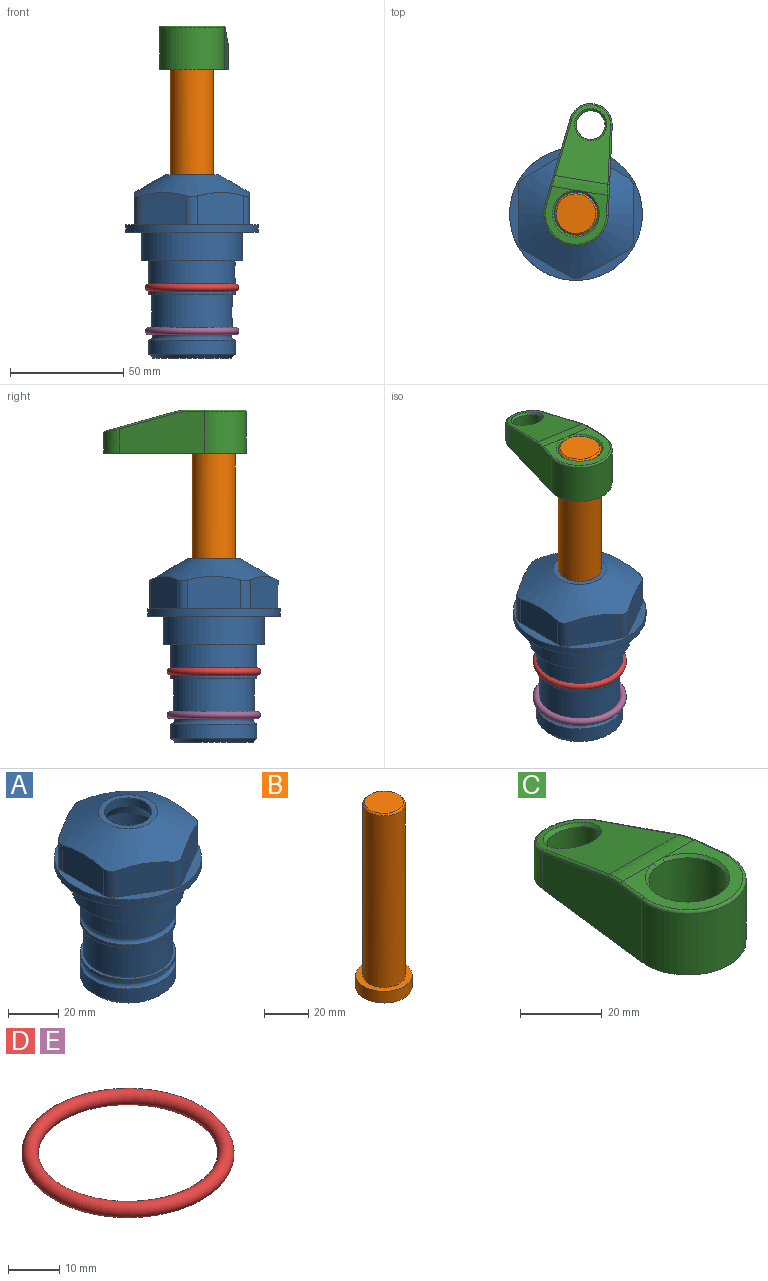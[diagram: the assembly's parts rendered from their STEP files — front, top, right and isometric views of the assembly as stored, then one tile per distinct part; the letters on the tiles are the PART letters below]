
ASSEMBLY  parts=5 mates=4
PART A: 36 faces, bbox 58.7x58.7x81 mm
  f0: cylinder r=17.78mm len=35.56mm, axis (0,0,1), area 1670.8mm2, adj f23,f24,f31
  f1: cylinder r=19.05mm len=38.1mm, axis (0,0,1), area 1191.9mm2, adj f26,f27,f30
  f2: plane 58.66x58.66mm, normal (0,0,-1), area 1150.6mm2, adj f3,f28
  f3: cylinder r=29.33mm len=58.66mm, axis (0,0,-1), area 585.1mm2, adj f2,f4
  f4: plane 58.66x58.66mm, normal (0,0,1), area 475.9mm2, adj f3,f5,f6,f7,f8,f9,f10,f11
  f5: plane 20.32x14.34mm, normal (-0.5,0.87,0), area 324.4mm2, adj f4,f15,f16,f17
  f6: plane 20.32x14.34mm, normal (0.5,0.87,0), area 324.4mm2, adj f4,f14,f15,f17
  f7: plane 23.48x14.34mm, normal (1,0,0), area 324.4mm2, adj f4,f13,f14,f17
  f8: plane 20.32x14.34mm, normal (0.5,-0.87,0), area 324.4mm2, adj f4,f12,f13,f17
  f9: plane 20.32x14.34mm, normal (-0.5,-0.87,0), area 324.4mm2, adj f4,f11,f12,f17
  f10: plane 23.48x14.34mm, normal (-1,0,0), area 324.4mm2, adj f4,f11,f16,f17
  f11: cylinder r=5.08mm len=12.85mm, axis (0,0,-1), area 67.2mm2, adj f4,f9,f10,f17
  f12: cylinder r=5.08mm len=12.85mm, axis (0,0,-1), area 67.2mm2, adj f4,f8,f9,f17
  f13: cylinder r=5.08mm len=12.85mm, axis (0,0,-1), area 67.2mm2, adj f4,f7,f8,f17
  f14: cylinder r=5.08mm len=12.85mm, axis (0,0,-1), area 67.2mm2, adj f4,f6,f7,f17
  f15: cylinder r=5.08mm len=12.85mm, axis (0,0,-1), area 67.2mm2, adj f4,f5,f6,f17
  f16: cylinder r=5.08mm len=12.85mm, axis (0,0,-1), area 67.2mm2, adj f4,f5,f10,f17
  f17: cone r=11.73mm half-angle=60deg, axis (0,0,-1), area 2071.8mm2, adj f5,f6,f7,f8,f9,f10,f11,f12
  f18: plane 23.46x23.46mm, normal (0,0,1), area 147.4mm2, adj f17,f35
  f19: plane 34.93x34.93mm, normal (0,0,-1), area 958mm2, adj f29
  f20: cylinder r=19.05mm len=38.1mm, axis (0,0,1), area 760.1mm2, adj f21,f29
  f21: torus R=19.05mm, axis (0,0,1), area 565.3mm2, adj f20,f22
  f22: cylinder r=19.05mm len=38.1mm, axis (0,0,1), area 190mm2, adj f21,f23
  f23: plane 38.1x38.1mm, normal (0,0,1), area 146.9mm2, adj f0,f22
  f24: plane 38.1x38.1mm, normal (0,0,-1), area 146.9mm2, adj f0,f25
  f25: cylinder r=19.05mm len=38.1mm, axis (0,0,1), area 190mm2, adj f24,f26
  f26: torus R=19.05mm, axis (0,0,1), area 565.3mm2, adj f1,f25
  f27: plane 44.45x44.45mm, normal (0,0,-1), area 411.7mm2, adj f1,f28
  f28: cylinder r=22.23mm len=44.45mm, axis (0,0,1), area 1773.5mm2, adj f2,f27
  f29: cone r=19.05mm half-angle=45deg, axis (0,0,1), area 257.5mm2, adj f19,f20
  f30: cylinder r=3.17mm len=6.75mm, axis (-1,0,0), area 128mm2, adj f1,f33
  f31: cylinder r=3.17mm len=6.35mm, axis (-1,0,0), area 102.5mm2, adj f0,f33
  f32: plane 25.4x25.4mm, normal (0,0,1), area 506.7mm2, adj f33
  f33: cylinder r=12.7mm len=66.42mm, axis (0,0,-1), area 5236.2mm2, adj f30,f31,f32,f34
  f34: cone r=9.53mm half-angle=30deg, axis (0,0,-1), area 443.4mm2, adj f33,f35
  f35: cylinder r=9.53mm len=19.05mm, axis (0,0,-1), area 240.9mm2, adj f18,f34
PART B: 6 faces, bbox 25.4x25.4x101.6 mm
  f0: plane 17.46x17.46mm, normal (0,0,1), area 239.5mm2, adj f5
  f1: plane 25.4x25.4mm, normal (0,0,-1), area 506.7mm2, adj f2
  f2: cylinder r=12.7mm len=25.4mm, axis (0,0,1), area 506.7mm2, adj f1,f3
  f3: plane 25.4x25.4mm, normal (0,0,1), area 221.7mm2, adj f2,f4
  f4: cylinder r=9.53mm len=94.46mm, axis (0,0,1), area 5653mm2, adj f3,f5
  f5: cone r=8.73mm half-angle=45deg, axis (0,0,-1), area 64.4mm2, adj f0,f4
PART C: 31 faces, bbox 31.7x65.5x19.8 mm
  f0: plane 39.12x18.26mm, normal (0.99,0.12,0), area 612.2mm2, adj f1,f4,f7,f11,f13,f15
  f1: cylinder r=9.53mm len=18.91mm, axis (0,0,-1), area 296.1mm2, adj f0,f2,f7,f17
  f2: plane 39.12x18.26mm, normal (-0.99,0.12,0), area 612.2mm2, adj f1,f4,f7,f12,f14,f16
  f3: cylinder r=6.35mm len=12.7mm, axis (0,0,-1), area 362.4mm2, adj f7,f18
  f4: cylinder r=14.29mm len=28.58mm, axis (0,0,-1), area 882.2mm2, adj f0,f2,f7,f10
  f5: cylinder r=9.53mm len=19.05mm, axis (0,0,-1), area 1092.6mm2, adj f7,f19,f20
  f6: plane 26.99x23.69mm, normal (0,0,1), area 216.2mm2, adj f9,f10,f11,f12,f19
  f7: plane 63.5x28.58mm, normal (0,0,-1), area 661.8mm2, adj f0,f1,f2,f3,f4,f5,f22,f23
  f8: plane 33.52x23.6mm, normal (0,0.26,0.97), area 486mm2, adj f9,f15,f16,f17,f18
  f9: cylinder r=19.05mm len=24.72mm, axis (1,0,0), area 120.4mm2, adj f6,f8,f13,f14,f20
  f10: torus R=13.49mm, axis (0,0,1), area 59mm2, adj f4,f6,f11,f12
  f11: cylinder r=0.79mm len=8.67mm, axis (0.12,-0.99,0), area 10.8mm2, adj f0,f6,f10,f13
  f12: cylinder r=0.79mm len=8.67mm, axis (0.12,0.99,0), area 10.8mm2, adj f2,f6,f10,f14
  f13: bspline ~4.95x1.42mm, area 6.1mm2, adj f0,f9,f11,f15
  f14: bspline ~4.95x1.42mm, area 6.1mm2, adj f2,f9,f12,f16
  f15: cylinder r=0.79mm len=25.95mm, axis (0.12,-0.96,0.26), area 32.9mm2, adj f0,f8,f13,f17
  f16: cylinder r=0.79mm len=25.95mm, axis (0.12,0.96,-0.26), area 32.9mm2, adj f2,f8,f14,f17
  f17: bspline ~18.91x8.38mm, area 30mm2, adj f1,f8,f15,f16
  f18: bspline ~14.29x14.29mm, area 48.3mm2, adj f3,f8
  f19: cone r=9.53mm half-angle=45deg, axis (0,0,1), area 66.5mm2, adj f5,f6,f20
  f20: bspline ~3.22x0.96mm, area 3.5mm2, adj f5,f9,f19
  f21: plane 2.75x2.72mm, normal (0,0,-1), area 2.9mm2, adj f23,f25,f28
  f22: plane 23.05x15.88mm, normal (-0.99,-0.12,0), area 323.6mm2, adj f7,f25,f26,f27,f28,f29
  f23: plane 23.05x15.88mm, normal (0.99,-0.12,0), area 323.6mm2, adj f7,f21,f25,f27,f28,f30
  f24: cylinder r=9.53mm len=10.69mm, axis (0,0,-1), area 114.7mm2, adj f7,f27,f29,f30
  f25: cylinder r=12.7mm len=20.59mm, axis (0,0,-1), area 381.1mm2, adj f7,f21,f22,f23,f26,f28
  f26: plane 2.75x2.72mm, normal (0,0,-1), area 2.9mm2, adj f22,f25,f28
  f27: plane 19.72x18.37mm, normal (0,-0.26,-0.97), area 291.8mm2, adj f22,f23,f24,f28,f29,f30
  f28: cylinder r=15.88mm len=19.92mm, axis (1,0,0), area 54.8mm2, adj f21,f22,f23,f25,f26,f27
  f29: cylinder r=1.59mm len=11mm, axis (0,0,-1), area 34.7mm2, adj f7,f22,f24,f27
  f30: cylinder r=1.59mm len=11mm, axis (0,0,-1), area 34.7mm2, adj f7,f23,f24,f27
PART D: 1 faces, bbox 44.7x44.7x3.2 mm
  f0: torus R=19.05mm, axis (0,0,1), area 1193.9mm2
PART E: same geometry as D
PLACE A at identity fixed
PLACE B rot(axis=(0,0,-1),9.4deg) t=(0,0,27.55)mm
PLACE C rot(axis=(0,0,-1),9.4deg) t=(0,0,27.55)mm
PLACE D at identity
PLACE E t=(0,0,-19.21)mm
MATE fastened E.f0 <-> A.f0  axis (0,0,1) through (0,0,-43.72)mm
MATE fastened C.f4 <-> B.f2  axis (0,0,1) through (0,0,91.05)mm
MATE fastened D.f0 <-> A.f0  axis (0,0,1) through (0,0,-24.51)mm
MATE cylindrical B.f2 <-> A.f0  axis (0,0,-1) through (0,0,-10.55)mm
